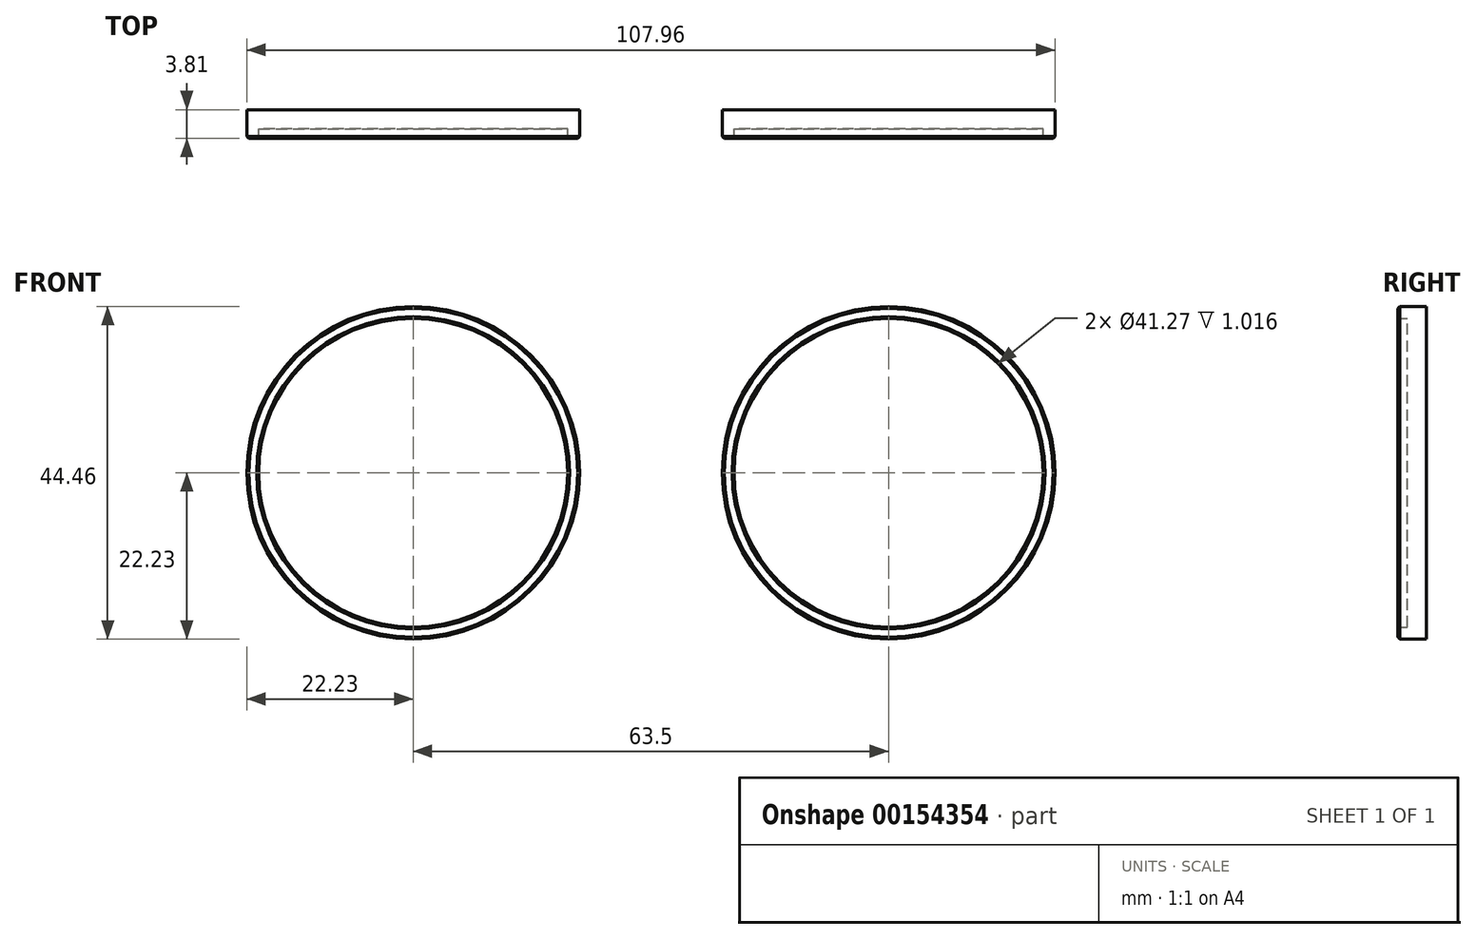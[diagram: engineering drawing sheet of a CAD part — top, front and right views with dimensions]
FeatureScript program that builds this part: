
annotation { "Feature Type Name" : "Feature", "Feature Type Description" : "" }
export const myFeature = defineFeature(function(context is Context, id is Id, definition is map)
    precondition{}
    {
        {
            var Q0;
            Q0=qCreatedBy(makeId("Front.planeOp"),FACE);
            var sketch = newSketch(context, id + "F0", { "sketchPlane" : qUnion([Q0])});
            skCircle(sketch, "E0", {"center": v(-31.75, 0) * mm, "radius": 20.64 * mm});
            skCircle(sketch, "E1", {"center": v(31.75, 0) * mm, "radius": 20.64 * mm});
            skCircle(sketch, "E2.0", {"center": v(-31.75, 0) * mm, "radius": 22.23 * mm});
            skCircle(sketch, "E3.0", {"center": v(31.75, 0) * mm, "radius": 22.23 * mm});
            skSolve(sketch);
        }
        {
            var Q0;
            Q0=makeQuery(id+"F0.imprint","IMPRINT",FACE,{"disambiguationData":[TD([[makeQuery(id+"F0.imprint","IMPRINT",EDGE,{"derivedFrom":sQuery(id+"F0.wireOp",EDGE,"E0")}),1.0]])]});
            var Q1;
            Q1=makeQuery(id+"F0.imprint","IMPRINT",FACE,{"disambiguationData":[TD([[makeQuery(id+"F0.imprint","IMPRINT",EDGE,{"derivedFrom":sQuery(id+"F0.wireOp",EDGE,"E1")}),1.0]])]});
            extrude(context, id + "F1", {"entities" : qUnion([Q0, Q1]), "depth" : 2.54 * mm});
        }
        {
            var Q0;
            Q0=makeQuery(id+"F0.imprint","IMPRINT",FACE,{"disambiguationData":[TD([[makeQuery(id+"F0.imprint","IMPRINT",EDGE,{"derivedFrom":sQuery(id+"F0.wireOp",EDGE,"E0")}),-1.0]])]});
            var Q1;
            Q1=makeQuery(id+"F0.imprint","IMPRINT",FACE,{"disambiguationData":[TD([[makeQuery(id+"F0.imprint","IMPRINT",EDGE,{"derivedFrom":sQuery(id+"F0.wireOp",EDGE,"E1")}),-1.0]])]});
            extrude(context, id + "F2", {"entities" : qUnion([Q0, Q1]), "operationType" : NewBodyOperationType.ADD, "depth" : 3.8 * mm});
        }
        {
            var Q0;
            Q0=makeQuery(id+"F2.opExtrude","CAP_EDGE",EDGE,{"disambiguationData":[OSD([sQuery(id+"F0.wireOp",EDGE,"E0")])],"isStart":false});
            var Q1;
            Q1=makeQuery(id+"F2.opExtrude","CAP_EDGE",EDGE,{"disambiguationData":[OSD([sQuery(id+"F0.wireOp",EDGE,"E2.0")])],"isStart":false});
            var Q2;
            Q2=makeQuery(id+"F2.opExtrude","CAP_EDGE",EDGE,{"disambiguationData":[OSD([sQuery(id+"F0.wireOp",EDGE,"E1")])],"isStart":false});
            var Q3;
            Q3=makeQuery(id+"F2.opExtrude","CAP_EDGE",EDGE,{"disambiguationData":[OSD([sQuery(id+"F0.wireOp",EDGE,"E3.0")])],"isStart":false});
            chamfer(context, id + "F3", {"entities" : qUnion([Q0, Q1, Q2, Q3]), "width" : 0.25 * mm, "tangentPropagation" : true});
        }
    });
